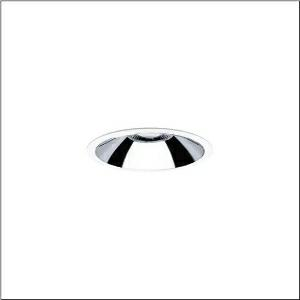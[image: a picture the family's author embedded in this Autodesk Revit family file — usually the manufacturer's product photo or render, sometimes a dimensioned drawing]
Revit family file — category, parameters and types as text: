
# Revit family: lunis_21_l_51db15md3c
name_source: partatom
category: Lighting Fixtures
units: mm (PartAtom-declared; Revit-internal decimal feet)

## family parameters
Cut with Voids When Loaded = No
Host = Face
Light Source = No
Part Type = Normal
Room Calculation Point = No
Round Connector Dimension = Use Diameter
Shared = No

## types (1)
- --- (1 x LED, 1670 lm, 13.8 W, 3000K)
    Apparent Load = 14 VA
    CIE Flux Codes = 90 99 100 100 100
    Color Rendering = 80
    Color Temperature = 3000K
    Default Elevation = 1800 mm
    Description = Lunis 21,  L, downlight, of PC, light emission: direct distribution, LED rated luminous flux: 1.670lm, light colour: 830, control gear: ECG, with terminal, 3-pole, mains connection: 220..240V, AC, housing, round, of diecast aluminium, traffic white (RAL 9016), diameter: 162mm, protection rating (complete): IP20, insulation class (complete): insulation class II (safety insulation), certification: CE, impact resistance: IK02, packaging unit: 1 piece
    Height = 0 mm  [stored 0 ft]
    Lamp = 1 x LED
    Lamp Light Flux = 1670 lm
    Lamp Power = 13.8 W
    Lamp count = 1
    Length = 162 mm
    Luminous efficacy = 121 lm/W
    Manufacturer = Siteco
    ModVariant = No
    Model = 51DB15MD3C
    Mounting Place = Ceiling
    Mounting Type = Recessed
    Number of Poles = 1
    OnlyDefault = Yes
    Power Factor = 1
    Product Name = Lunis 21 L
    Product group = downlight | ceiling recessed
    ProductGroupID = 402
    Protection Class = Protection class II
    Protection Degree = IP 20
    RLX_Detail_Level = 1
    RlxData = <blob elided: 21881 chars, md5=dd66872c>
    Socket = socket
    Standby Power = 0 W
    System Light Flux = 1670 lm
    System Power = 14 W
    Type Comments = factory setting: luminous flux: 100 % | (ON | ON)
    Type Image = l_1006992.jpg
    URL = http://relux.com
    VarID = @adj_078313
    Voltage = 0 V
    Weight = 0.00 kg
    Width = 0 mm  [stored 0 ft]

note: [stored X ft] marks values corroborated as IEEE doubles in the binary element streams (Revit-internal decimal feet)

## geometry (parser evidence)
native form markers: Blend x4, Sweep x10
no freeform markers — native parametric forms only
